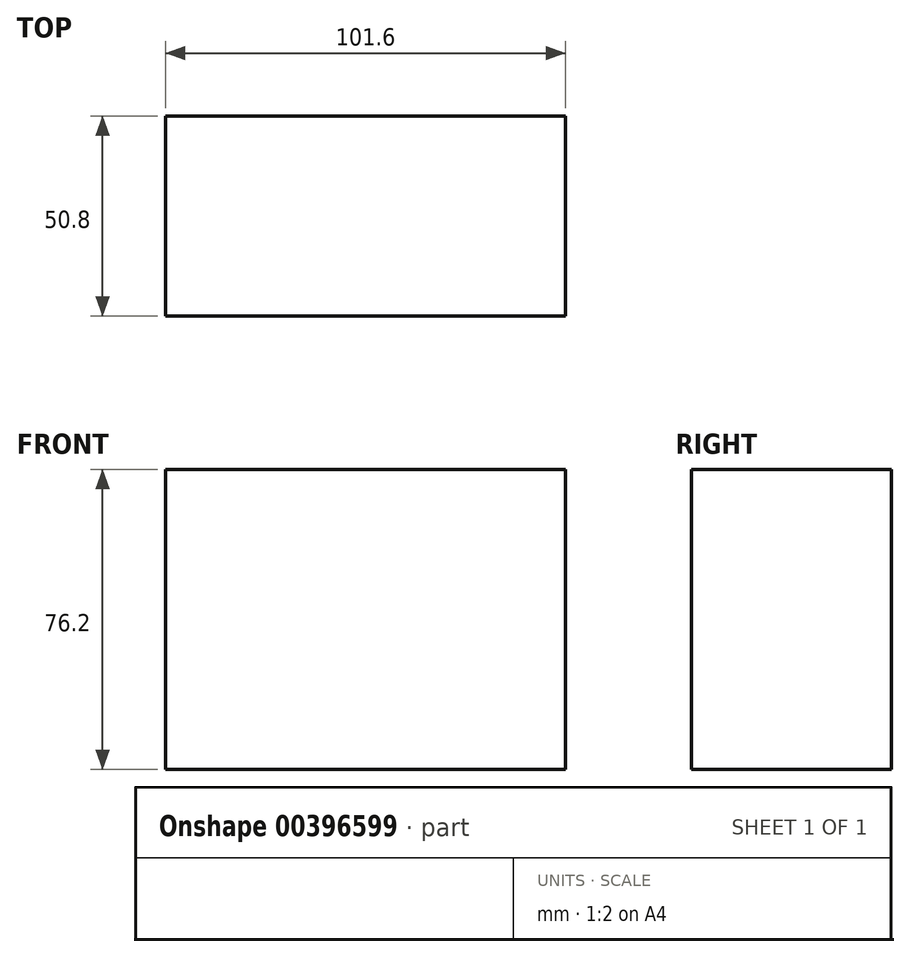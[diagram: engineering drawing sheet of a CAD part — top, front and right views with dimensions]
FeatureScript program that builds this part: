
annotation { "Feature Type Name" : "Feature", "Feature Type Description" : "" }
export const myFeature = defineFeature(function(context is Context, id is Id, definition is map)
    precondition{}
    {
        {
            var Q0;
            Q0=qCreatedBy(makeId("Front.planeOp"),FACE);
            var sketch = newSketch(context, id + "F0", { "sketchPlane" : qUnion([Q0])});
            skSolve(sketch);
        }
        {
            var Q0;
            Q0=qCreatedBy(makeId("Front.planeOp"),FACE);
            var sketch = newSketch(context, id + "F1", { "sketchPlane" : qUnion([Q0])});
            skLineSegment(sketch, "E0.bottom", {"start": v(-50.8, 38.1) * mm, "end": v(50.8, 38.1) * mm});
            skLineSegment(sketch, "E0.top", {"start": v(-50.8, -38.1) * mm, "end": v(50.8, -38.1) * mm});
            skLineSegment(sketch, "E0.left", {"start": v(-50.8, 38.1) * mm, "end": v(-50.8, -38.1) * mm});
            skLineSegment(sketch, "E0.right", {"start": v(50.8, 38.1) * mm, "end": v(50.8, -38.1) * mm});
            skPoint(sketch, "E0.middle", {"position": v(0, 0) * mm});
            skSolve(sketch);
        }
        {
            var Q0;
            Q0 = qSketchRegion(id + "F0", true);
            var Q1;
            Q1 = qSketchRegion(id + "F1", true);
            var Q2;
            Q2 = qSketchRegion(id + "FZp9qHshfbVK947_0", true);
            extrude(context, id + "F2", {"entities" : qUnion([Q0, Q1, Q2]), "depth" : 50.8 * mm});
        }
    });
